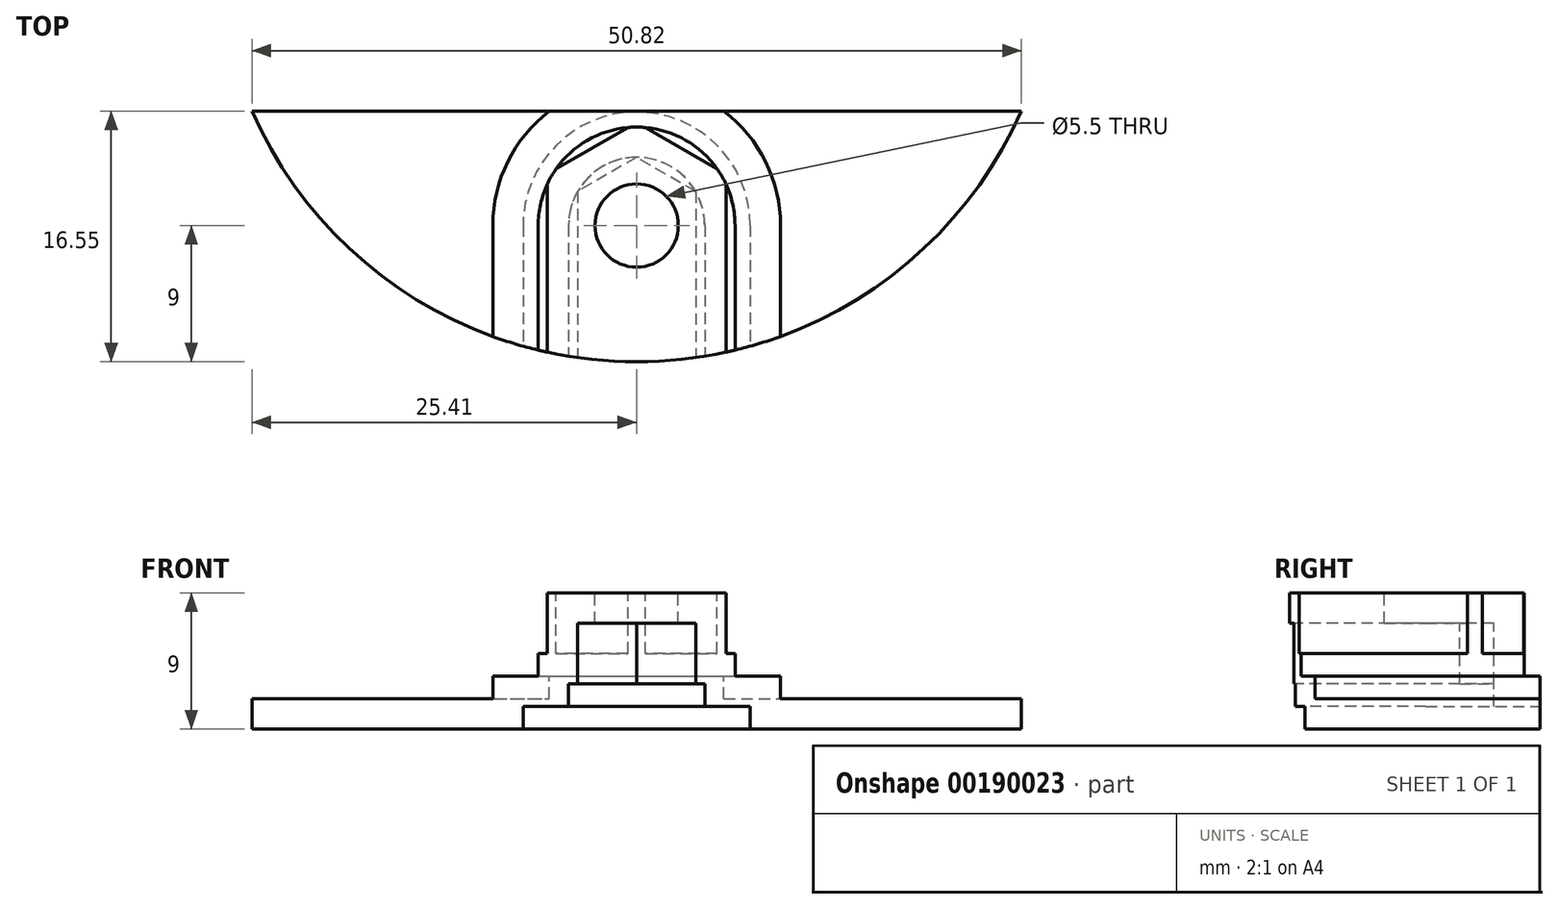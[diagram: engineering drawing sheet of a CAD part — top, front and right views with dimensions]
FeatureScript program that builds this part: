
annotation { "Feature Type Name" : "Feature", "Feature Type Description" : "" }
export const myFeature = defineFeature(function(context is Context, id is Id, definition is map)
    precondition{}
    {
        {
            var Q0;
            Q0=qCreatedBy(makeId("Top.planeOp"),FACE);
            var sketch = newSketch(context, id + "F0", { "sketchPlane" : qUnion([Q0])});
            skLineSegment(sketch, "E0", {"start": v(-26, 0) * mm, "end": v(26, 0) * mm, "construction": true});
            skLineSegment(sketch, "E1", {"start": v(0, 0) * mm, "end": v(0, -18) * mm, "construction": true});
            skArc(sketch, "E2", {"start": v(-26, 0) * mm, "mid": v(0, -18) * mm, "end": v(26, 0) * mm});
            skLineSegment(sketch, "E3.0", {"start": v(-25.4, -1.45) * mm, "end": v(25.4, -1.45) * mm});
            skPoint(sketch, "E4", {"position": v(0, -9) * mm});
            skCircle(sketch, "E5", {"center": v(0, -9) * mm, "radius": 2.75 * mm});
            skSolve(sketch);
        }
        {
            var Q0;
            Q0 = qSketchRegion(id + "F0", true);
            extrude(context, id + "F1", {"entities" : qUnion([Q0]), "oppositeDirection" : true, "depth" : 2 * mm});
        }
        {
            var Q0;
            Q0=makeQuery(id+"F1.opExtrude","CAP_FACE",FACE,{"disambiguationData":[OSD([sQuery(id+"F0.wireOp",EDGE,"E2"),sQuery(id+"F0.wireOp",EDGE,"E3.0"),sQuery(id+"F0.wireOp",EDGE,"E5")])],"isStart":false});
            var sketch = newSketch(context, id + "F2", { "sketchPlane" : qUnion([Q0])});
            skArc(sketch, "E6.0", {"start": v(-26, 0) * mm, "mid": v(0, 18) * mm, "end": v(26, 0) * mm});
            skLineSegment(sketch, "E7.0", {"start": v(-25.4, 1.45) * mm, "end": v(25.4, 1.45) * mm});
            skPoint(sketch, "E8.0", {"position": v(0, 9) * mm});
            skCircle(sketch, "E9.cCircle", {"center": v(0, 9) * mm, "radius": 4.5 * mm, "construction": true});
            skPoint(sketch, "E9.cCircle.perimeterSnap0", {"position": v(0, 1.45) * mm});
            skLineSegment(sketch, "E9.0", {"start": v(0, 4.5) * mm, "end": v(-3.9, 6.75) * mm});
            skPoint(sketch, "E9.0.startSnap0", {"position": v(0, 1.45) * mm});
            skLineSegment(sketch, "E9.1", {"start": v(-3.9, 6.75) * mm, "end": v(-3.9, 11.25) * mm});
            skLineSegment(sketch, "E9.2", {"start": v(-3.9, 11.25) * mm, "end": v(0, 13.5) * mm});
            skLineSegment(sketch, "E9.3", {"start": v(0, 13.5) * mm, "end": v(3.9, 11.25) * mm});
            skLineSegment(sketch, "E9.4", {"start": v(3.9, 11.25) * mm, "end": v(3.9, 6.75) * mm});
            skLineSegment(sketch, "E9.5", {"start": v(3.9, 6.75) * mm, "end": v(0, 4.5) * mm});
            skLineSegment(sketch, "E10", {"start": v(-3.9, 11.25) * mm, "end": v(-3.9, 17.73) * mm});
            skLineSegment(sketch, "E11", {"start": v(3.9, 11.25) * mm, "end": v(3.9, 17.73) * mm});
            skSolve(sketch);
        }
        {
            var Q0;
            {var subQ1=sQuery(id+"F2.wireOp",EDGE,"E7.0");Q0=makeQuery(id+"F2.imprint","IMPRINT",FACE,{"disambiguationData":[TD([[makeQuery(id+"F2.imprint","IMPRINT",EDGE,{"derivedFrom":subQ1}),1.0]])]});}
            extrude(context, id + "F3", {"entities" : qUnion([Q0]), "operationType" : NewBodyOperationType.ADD, "depth" : 4 * mm});
        }
        {
            var Q0;
            Q0=makeQuery(id+"F3.opExtrude","CAP_FACE",FACE,{"disambiguationData":[OSD([sQuery(id+"F2.wireOp",EDGE,"E6.0"),sQuery(id+"F2.wireOp",EDGE,"E7.0"),sQuery(id+"F2.wireOp",EDGE,"E9.0"),sQuery(id+"F2.wireOp",EDGE,"E9.1"),sQuery(id+"F2.wireOp",EDGE,"E9.4"),sQuery(id+"F2.wireOp",EDGE,"E9.5"),sQuery(id+"F2.wireOp",EDGE,"E10"),sQuery(id+"F2.wireOp",EDGE,"E11")])],"isStart":false});
            var sketch = newSketch(context, id + "F4", { "sketchPlane" : qUnion([Q0])});
            skArc(sketch, "E12.0", {"start": v(-26, 0) * mm, "mid": v(0, 18) * mm, "end": v(26, 0) * mm});
            skLineSegment(sketch, "E13.0", {"start": v(-25.4, 1.45) * mm, "end": v(25.4, 1.45) * mm});
            skPoint(sketch, "E14.0", {"position": v(0, 9) * mm});
            skCircle(sketch, "E15", {"center": v(0, 9) * mm, "radius": 4.5 * mm});
            skLineSegment(sketch, "E16", {"start": v(-4.5, 9) * mm, "end": v(-4.5, 17.73) * mm});
            skLineSegment(sketch, "E17", {"start": v(4.5, 9) * mm, "end": v(4.5, 17.63) * mm});
            skSolve(sketch);
        }
        {
            var Q0;
            {var subQ8=sQuery(id+"F4.wireOp",EDGE,"E13.0");Q0=makeQuery(id+"F4.imprint","IMPRINT",FACE,{"disambiguationData":[TD([[makeQuery(id+"F4.imprint","IMPRINT",EDGE,{"derivedFrom":subQ8}),1.0]])]});}
            extrude(context, id + "F5", {"entities" : qUnion([Q0]), "operationType" : NewBodyOperationType.ADD, "depth" : 1.5 * mm});
        }
        {
            var Q0;
            Q0=makeQuery(id+"F5.opExtrude","CAP_FACE",FACE,{"disambiguationData":[OSD([sQuery(id+"F4.wireOp",EDGE,"E12.0"),sQuery(id+"F4.wireOp",EDGE,"E13.0"),sQuery(id+"F4.wireOp",EDGE,"E15"),sQuery(id+"F4.wireOp",EDGE,"E16"),sQuery(id+"F4.wireOp",EDGE,"E17")])],"isStart":false});
            var sketch = newSketch(context, id + "F6", { "sketchPlane" : qUnion([Q0])});
            skArc(sketch, "E18.0", {"start": v(-26, 0) * mm, "mid": v(0, 18) * mm, "end": v(26, 0) * mm});
            skLineSegment(sketch, "E19.0", {"start": v(-25.4, 1.45) * mm, "end": v(25.4, 1.45) * mm});
            skPoint(sketch, "E20.0", {"position": v(0, 9) * mm});
            skCircle(sketch, "E21", {"center": v(0, 9) * mm, "radius": 7.5 * mm});
            skLineSegment(sketch, "E22", {"start": v(-7.5, 9) * mm, "end": v(-7.5, 16.97) * mm});
            skLineSegment(sketch, "E23", {"start": v(7.5, 9) * mm, "end": v(7.5, 16.97) * mm});
            skSolve(sketch);
        }
        {
            var Q0;
            {var subQ3=sQuery(id+"F6.wireOp",EDGE,"E23");Q0=makeQuery(id+"F6.imprint","IMPRINT",FACE,{"disambiguationData":[TD([[makeQuery(id+"F6.imprint","IMPRINT",EDGE,{"derivedFrom":subQ3}),-1.0]])]});}
            extrude(context, id + "F7", {"entities" : qUnion([Q0]), "operationType" : NewBodyOperationType.ADD, "depth" : 1.5 * mm});
        }
        {
            var Q0;
            Q0=makeQuery(id+"F1.opExtrude","CAP_FACE",FACE,{"disambiguationData":[OSD([sQuery(id+"F0.wireOp",EDGE,"E2"),sQuery(id+"F0.wireOp",EDGE,"E3.0"),sQuery(id+"F0.wireOp",EDGE,"E5")])],"isStart":true});
            var Q1;
            {var subQ0=sQuery(id+"F6.wireOp",EDGE,"E19.0");var subQ1=sQuery(id+"F6.wireOp",EDGE,"E18.0");var subQ2=sQuery(id+"F4.wireOp",EDGE,"E13.0");var subQ3=sQuery(id+"F4.wireOp",EDGE,"E12.0");var subQ4=sQuery(id+"F2.wireOp",EDGE,"E7.0");var subQ5=sQuery(id+"F2.wireOp",EDGE,"E6.0");Q1=makeQuery(id+"F7.boolean.opBoolean","MERGE",FACE,{"derivedFrom":[makeQuery(id+"F5.boolean.opBoolean","MERGE",FACE,{"derivedFrom":[makeQuery(id+"F3.boolean.opBoolean","MERGE",FACE,{"derivedFrom":[makeQuery(id+"F1.opExtrude","SWEPT_FACE",FACE,{"disambiguationData":[OSD([sQuery(id+"F0.wireOp",EDGE,"E2")])]}),makeQuery(id+"F3.opExtrude","SWEPT_FACE",FACE,{"disambiguationData":[OSD([subQ5]),TDD([makeQuery(id+"F2.imprint","IMPRINT",EDGE,{"disambiguationData":[TD([[makeQuery(id+"F2.imprint","INTERSECT",VERTEX,{"disambiguationData":[OD(0.0)],"derivedFrom":[subQ5,subQ4]}),-1.0]])],"derivedFrom":subQ5})])]}),makeQuery(id+"F3.opExtrude","SWEPT_FACE",FACE,{"disambiguationData":[OSD([subQ5]),TDD([makeQuery(id+"F2.imprint","IMPRINT",EDGE,{"disambiguationData":[TD([[makeQuery(id+"F2.imprint","INTERSECT",VERTEX,{"disambiguationData":[OD(1.0)],"derivedFrom":[subQ5,subQ4]}),1.0]])],"derivedFrom":subQ5})])]})]}),makeQuery(id+"F5.opExtrude","SWEPT_FACE",FACE,{"disambiguationData":[OSD([subQ3]),TDD([makeQuery(id+"F4.imprint","IMPRINT",EDGE,{"disambiguationData":[TD([[makeQuery(id+"F4.imprint","INTERSECT",VERTEX,{"disambiguationData":[OD(0.0)],"derivedFrom":[subQ3,subQ2]}),-1.0]])],"derivedFrom":subQ3})])]}),makeQuery(id+"F5.opExtrude","SWEPT_FACE",FACE,{"disambiguationData":[OSD([subQ3]),TDD([makeQuery(id+"F4.imprint","IMPRINT",EDGE,{"disambiguationData":[TD([[makeQuery(id+"F4.imprint","INTERSECT",VERTEX,{"disambiguationData":[OD(1.0)],"derivedFrom":[subQ3,subQ2]}),1.0]])],"derivedFrom":subQ3})])]})]}),makeQuery(id+"F7.opExtrude","SWEPT_FACE",FACE,{"disambiguationData":[OSD([subQ1]),TDD([makeQuery(id+"F6.imprint","IMPRINT",EDGE,{"disambiguationData":[TD([[makeQuery(id+"F6.imprint","INTERSECT",VERTEX,{"disambiguationData":[OD(0.0)],"derivedFrom":[subQ1,subQ0]}),-1.0]])],"derivedFrom":subQ1})])]}),makeQuery(id+"F7.opExtrude","SWEPT_FACE",FACE,{"disambiguationData":[OSD([subQ1]),TDD([makeQuery(id+"F6.imprint","IMPRINT",EDGE,{"disambiguationData":[TD([[makeQuery(id+"F6.imprint","INTERSECT",VERTEX,{"disambiguationData":[OD(1.0)],"derivedFrom":[subQ1,subQ0]}),1.0]])],"derivedFrom":subQ1})])]})]});}
            var Q2;
            Q2=makeQuery(id+"F7.boolean.opBoolean","MERGE",FACE,{"derivedFrom":[makeQuery(id+"F5.boolean.opBoolean","MERGE",FACE,{"derivedFrom":[makeQuery(id+"F3.boolean.opBoolean","MERGE",FACE,{"derivedFrom":[makeQuery(id+"F1.opExtrude","SWEPT_FACE",FACE,{"disambiguationData":[OSD([sQuery(id+"F0.wireOp",EDGE,"E3.0")])]}),makeQuery(id+"F3.opExtrude","SWEPT_FACE",FACE,{"disambiguationData":[OSD([sQuery(id+"F2.wireOp",EDGE,"E7.0")])]})]}),makeQuery(id+"F5.opExtrude","SWEPT_FACE",FACE,{"disambiguationData":[OSD([sQuery(id+"F4.wireOp",EDGE,"E13.0")])]})]}),makeQuery(id+"F7.opExtrude","SWEPT_FACE",FACE,{"disambiguationData":[OSD([sQuery(id+"F6.wireOp",EDGE,"E19.0")])]})]});
            shell(context, id + "F8", {"entities" : qUnion([Q0, Q1, Q2]), "thickness" : 2 * mm});
        }
    });
